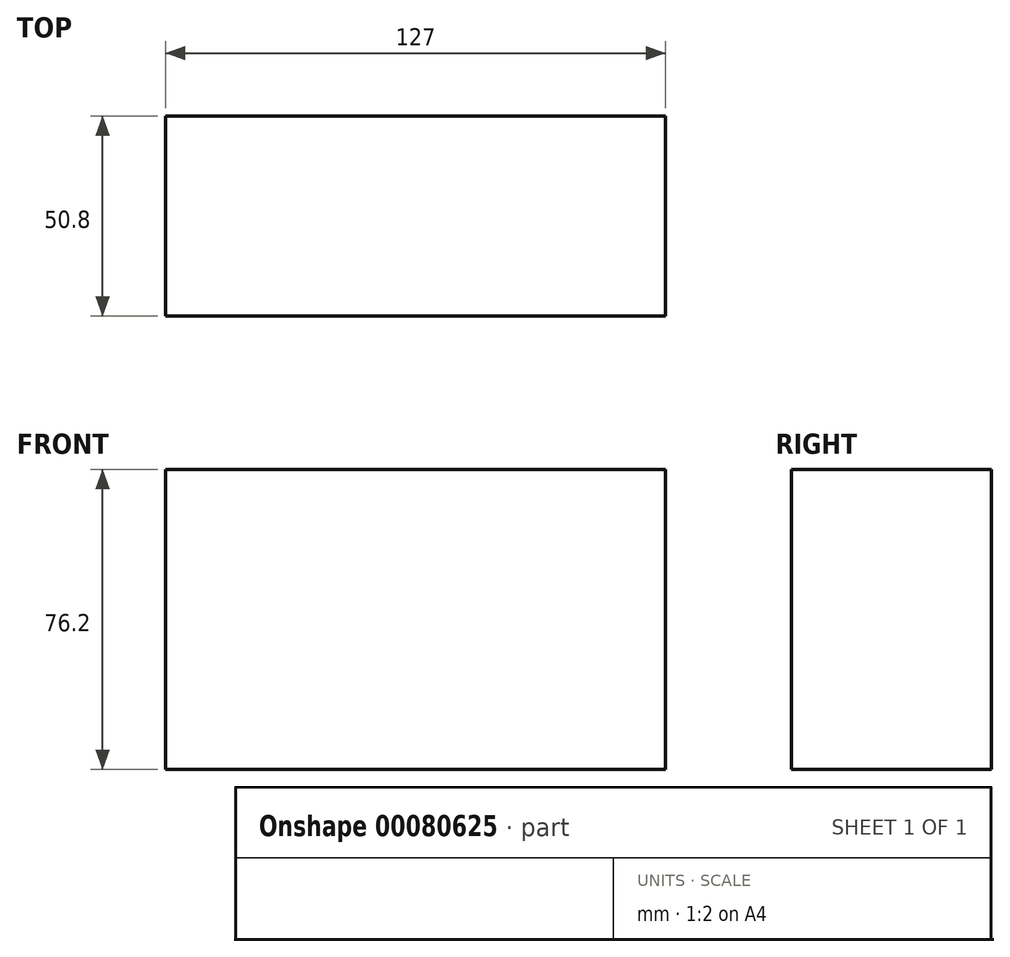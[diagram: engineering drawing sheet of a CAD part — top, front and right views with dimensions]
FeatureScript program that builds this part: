
annotation { "Feature Type Name" : "Feature", "Feature Type Description" : "" }
export const myFeature = defineFeature(function(context is Context, id is Id, definition is map)
    precondition{}
    {
        {
            var Q0;
            Q0=qCreatedBy(makeId("Front.planeOp"),FACE);
            var sketch = newSketch(context, id + "F0", { "sketchPlane" : qUnion([Q0])});
            skLineSegment(sketch, "E0", {"start": v(0, 0) * mm, "end": v(127, 0) * mm});
            skLineSegment(sketch, "E1", {"start": v(127, 0) * mm, "end": v(127, 76.2) * mm});
            skLineSegment(sketch, "E2", {"start": v(127, 76.2) * mm, "end": v(0, 76.2) * mm});
            skLineSegment(sketch, "E3", {"start": v(0, 76.2) * mm, "end": v(0, 0) * mm});
            skSolve(sketch);
        }
        {
            var Q0;
            Q0=makeQuery(id+"F0.imprint","IMPRINT",FACE,{"disambiguationData":[TD([[makeQuery(id+"F0.imprint","IMPRINT",EDGE,{"derivedFrom":sQuery(id+"F0.wireOp",EDGE,"E0")}),1.0]])]});
            extrude(context, id + "F1", {"entities" : qUnion([Q0]), "depth" : 50.8 * mm});
        }
    });
